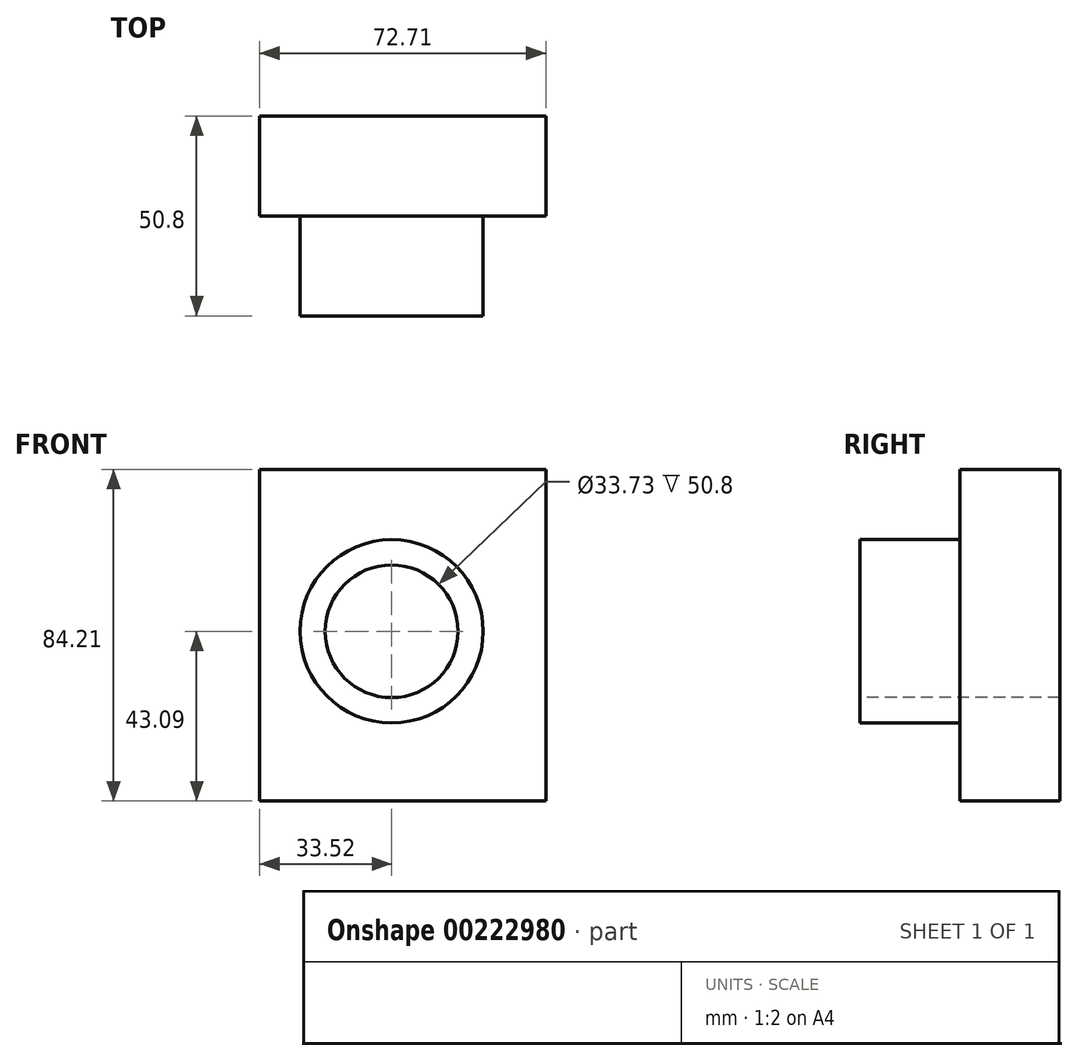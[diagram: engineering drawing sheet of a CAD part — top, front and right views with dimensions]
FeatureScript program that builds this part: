
annotation { "Feature Type Name" : "Feature", "Feature Type Description" : "" }
export const myFeature = defineFeature(function(context is Context, id is Id, definition is map)
    precondition{}
    {
        {
            var Q0;
            Q0=qCreatedBy(makeId("Front.planeOp"),FACE);
            var sketch = newSketch(context, id + "F0", { "sketchPlane" : qUnion([Q0])});
            skLineSegment(sketch, "E0.bottom", {"start": v(-33.52, 41.12) * mm, "end": v(39.2, 41.12) * mm});
            skLineSegment(sketch, "E0.top", {"start": v(-33.52, -43.1) * mm, "end": v(39.2, -43.1) * mm});
            skLineSegment(sketch, "E0.left", {"start": v(-33.52, 41.12) * mm, "end": v(-33.52, -43.1) * mm});
            skLineSegment(sketch, "E0.right", {"start": v(39.2, 41.12) * mm, "end": v(39.2, -43.1) * mm});
            skSolve(sketch);
        }
        {
            var Q0;
            Q0 = qSketchRegion(id + "F0", true);
            extrude(context, id + "F1", {"entities" : qUnion([Q0]), "depth" : 25.4 * mm});
        }
        {
            var Q0;
            Q0=qCreatedBy(makeId("Front.planeOp"),FACE);
            var sketch = newSketch(context, id + "F2", { "sketchPlane" : qUnion([Q0])});
            skCircle(sketch, "E1", {"center": v(0, 0) * mm, "radius": 23.27 * mm});
            skSolve(sketch);
        }
        {
            var Q0;
            Q0 = qSketchRegion(id + "F2", true);
            extrude(context, id + "F3", {"entities" : qUnion([Q0]), "operationType" : NewBodyOperationType.ADD, "depth" : 50.8 * mm});
        }
        {
            var Q0;
            Q0=makeQuery(id+"F3.opExtrude","CAP_FACE",FACE,{"disambiguationData":[OSD([sQuery(id+"F2.wireOp",EDGE,"E1")])],"isStart":false});
            var sketch = newSketch(context, id + "F4", { "sketchPlane" : qUnion([Q0])});
            skCircle(sketch, "E2", {"center": v(0, 0) * mm, "radius": 16.86 * mm});
            skCircle(sketch, "E3.0", {"center": v(0, 0) * mm, "radius": 23.27 * mm});
            skSolve(sketch);
        }
        {
            var Q0;
            Q0=makeQuery(id+"F4.imprint","IMPRINT",FACE,{"disambiguationData":[TD([[makeQuery(id+"F4.imprint","IMPRINT",EDGE,{"derivedFrom":sQuery(id+"F4.wireOp",EDGE,"E2")}),1.0]])]});
            extrude(context, id + "F5", {"entities" : qUnion([Q0]), "operationType" : NewBodyOperationType.REMOVE, "endBound" : BoundingType.THROUGH_ALL, "oppositeDirection" : true, "depth" : 25.4 * mm});
        }
    });
